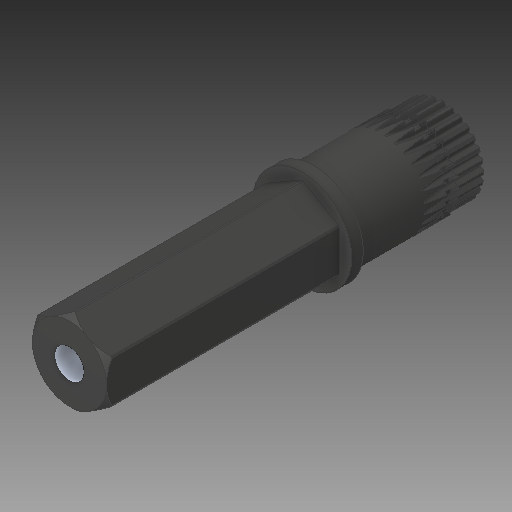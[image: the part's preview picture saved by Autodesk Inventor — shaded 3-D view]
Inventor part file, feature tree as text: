
AUTODESK INVENTOR PART (.ipt)
format: ipt  version: 2017 (Build 210142000, 142)  size: 1,423,360 bytes
history: native  units: in
note: dims shown in document units (in); Inventor stores cm internally (conversion verified against a paired STEP export)
features: fillet x1
ambient origin geometry x8: Origin, YZ Plane, XZ Plane, XY Plane, X Axis, Y Axis, Z Axis, Center Point
bodies: Solid1 (feature_tree)
feature tree (1):
  fillet  "Fillet5"  [1 undecoded]
note: 1 required parameter value undecoded (feature->parameter linkage not recoverable at this tier; creation-order binding heuristic only, values carry confidence <= 0.55)
